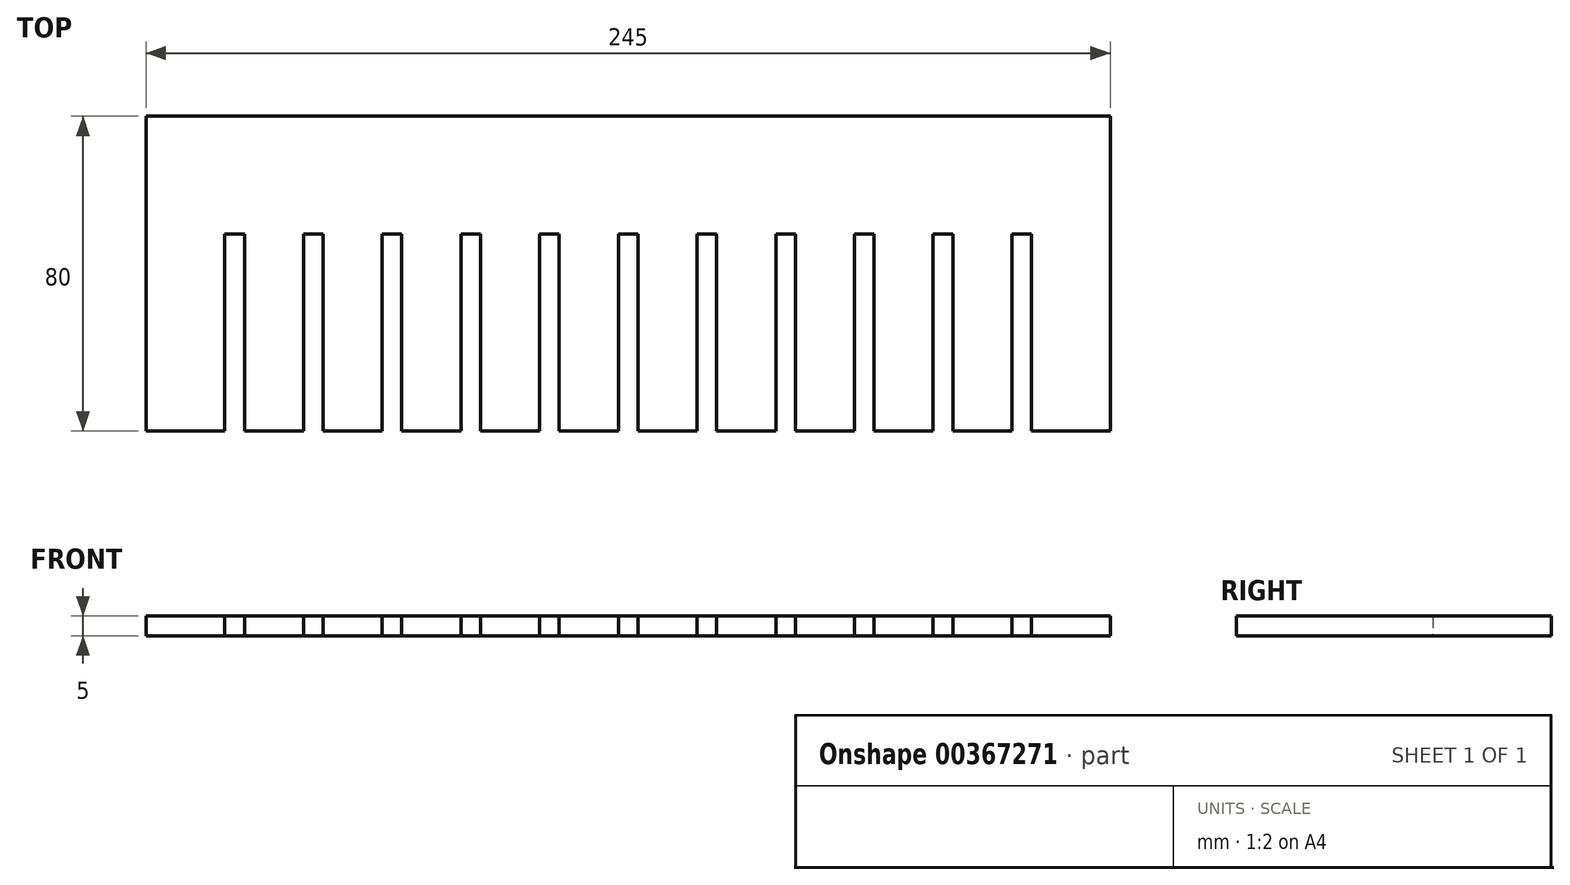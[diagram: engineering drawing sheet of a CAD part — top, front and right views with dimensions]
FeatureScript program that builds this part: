
annotation { "Feature Type Name" : "Feature", "Feature Type Description" : "" }
export const myFeature = defineFeature(function(context is Context, id is Id, definition is map)
    precondition{}
    {
        {
            var Q0;
            Q0=qCreatedBy(makeId("Top.planeOp"),FACE);
            var sketch = newSketch(context, id + "F0", { "sketchPlane" : qUnion([Q0])});
            skLineSegment(sketch, "E0", {"start": v(0, 0) * mm, "end": v(0, 80) * mm});
            skLineSegment(sketch, "E1", {"start": v(0, 0) * mm, "end": v(20, 0) * mm});
            skLineSegment(sketch, "E2", {"start": v(20, 0) * mm, "end": v(20, 50) * mm});
            skLineSegment(sketch, "E3", {"start": v(20, 50) * mm, "end": v(22.5, 50) * mm});
            skLineSegment(sketch, "E4", {"start": v(22.5, 50) * mm, "end": v(25, 50) * mm});
            skLineSegment(sketch, "E5", {"start": v(25, 50) * mm, "end": v(25, 0) * mm});
            skLineSegment(sketch, "E6", {"start": v(25, 0) * mm, "end": v(40, 0) * mm});
            skLineSegment(sketch, "E7", {"start": v(40, 0) * mm, "end": v(40, 50) * mm});
            skLineSegment(sketch, "E8", {"start": v(40, 50) * mm, "end": v(42.5, 50) * mm});
            skLineSegment(sketch, "E9.1.0.0", {"start": v(60, 0) * mm, "end": v(60, 50) * mm});
            skLineSegment(sketch, "E9.1.0.1", {"start": v(45, 0) * mm, "end": v(60, 0) * mm});
            skLineSegment(sketch, "E9.1.0.2", {"start": v(45, 50) * mm, "end": v(45, 0) * mm});
            skLineSegment(sketch, "E9.1.0.3", {"start": v(60, 50) * mm, "end": v(62.5, 50) * mm});
            skLineSegment(sketch, "E9.1.0.4", {"start": v(42.5, 50) * mm, "end": v(45, 50) * mm});
            skLineSegment(sketch, "E9.2.0.0", {"start": v(80, 0) * mm, "end": v(80, 50) * mm});
            skLineSegment(sketch, "E9.2.0.1", {"start": v(65, 0) * mm, "end": v(80, 0) * mm});
            skLineSegment(sketch, "E9.2.0.2", {"start": v(65, 50) * mm, "end": v(65, 0) * mm});
            skLineSegment(sketch, "E9.2.0.3", {"start": v(80, 50) * mm, "end": v(82.5, 50) * mm});
            skLineSegment(sketch, "E9.2.0.4", {"start": v(62.5, 50) * mm, "end": v(65, 50) * mm});
            skLineSegment(sketch, "E9.3.0.0", {"start": v(100, 0) * mm, "end": v(100, 50) * mm});
            skLineSegment(sketch, "E9.3.0.1", {"start": v(85, 0) * mm, "end": v(100, 0) * mm});
            skLineSegment(sketch, "E9.3.0.2", {"start": v(85, 50) * mm, "end": v(85, 0) * mm});
            skLineSegment(sketch, "E9.3.0.3", {"start": v(100, 50) * mm, "end": v(102.5, 50) * mm});
            skLineSegment(sketch, "E9.3.0.4", {"start": v(82.5, 50) * mm, "end": v(85, 50) * mm});
            skLineSegment(sketch, "E9.4.0.0", {"start": v(120, 0) * mm, "end": v(120, 50) * mm});
            skLineSegment(sketch, "E9.4.0.1", {"start": v(105, 0) * mm, "end": v(120, 0) * mm});
            skLineSegment(sketch, "E9.4.0.2", {"start": v(105, 50) * mm, "end": v(105, 0) * mm});
            skLineSegment(sketch, "E9.4.0.3", {"start": v(120, 50) * mm, "end": v(122.5, 50) * mm});
            skLineSegment(sketch, "E9.4.0.4", {"start": v(102.5, 50) * mm, "end": v(105, 50) * mm});
            skLineSegment(sketch, "E9.5.0.0", {"start": v(140, 0) * mm, "end": v(140, 50) * mm});
            skLineSegment(sketch, "E9.5.0.1", {"start": v(125, 0) * mm, "end": v(140, 0) * mm});
            skLineSegment(sketch, "E9.5.0.2", {"start": v(125, 50) * mm, "end": v(125, 0) * mm});
            skLineSegment(sketch, "E9.5.0.3", {"start": v(140, 50) * mm, "end": v(142.5, 50) * mm});
            skLineSegment(sketch, "E9.5.0.4", {"start": v(122.5, 50) * mm, "end": v(125, 50) * mm});
            skLineSegment(sketch, "E9.6.0.0", {"start": v(160, 0) * mm, "end": v(160, 50) * mm});
            skLineSegment(sketch, "E9.6.0.1", {"start": v(145, 0) * mm, "end": v(160, 0) * mm});
            skLineSegment(sketch, "E9.6.0.2", {"start": v(145, 50) * mm, "end": v(145, 0) * mm});
            skLineSegment(sketch, "E9.6.0.3", {"start": v(160, 50) * mm, "end": v(162.5, 50) * mm});
            skLineSegment(sketch, "E9.6.0.4", {"start": v(142.5, 50) * mm, "end": v(145, 50) * mm});
            skLineSegment(sketch, "E9.7.0.0", {"start": v(180, 0) * mm, "end": v(180, 50) * mm});
            skLineSegment(sketch, "E9.7.0.1", {"start": v(165, 0) * mm, "end": v(180, 0) * mm});
            skLineSegment(sketch, "E9.7.0.2", {"start": v(165, 50) * mm, "end": v(165, 0) * mm});
            skLineSegment(sketch, "E9.7.0.3", {"start": v(180, 50) * mm, "end": v(182.5, 50) * mm});
            skLineSegment(sketch, "E9.7.0.4", {"start": v(162.5, 50) * mm, "end": v(165, 50) * mm});
            skLineSegment(sketch, "E9.8.0.0", {"start": v(200, 0) * mm, "end": v(200, 50) * mm});
            skLineSegment(sketch, "E9.8.0.1", {"start": v(185, 0) * mm, "end": v(200, 0) * mm});
            skLineSegment(sketch, "E9.8.0.2", {"start": v(185, 50) * mm, "end": v(185, 0) * mm});
            skLineSegment(sketch, "E9.8.0.3", {"start": v(200, 50) * mm, "end": v(202.5, 50) * mm});
            skLineSegment(sketch, "E9.8.0.4", {"start": v(182.5, 50) * mm, "end": v(185, 50) * mm});
            skLineSegment(sketch, "E9.9.0.0", {"start": v(220, 0) * mm, "end": v(220, 50) * mm});
            skLineSegment(sketch, "E9.9.0.1", {"start": v(205, 0) * mm, "end": v(220, 0) * mm});
            skLineSegment(sketch, "E9.9.0.2", {"start": v(205, 50) * mm, "end": v(205, 0) * mm});
            skLineSegment(sketch, "E9.9.0.3", {"start": v(220, 50) * mm, "end": v(222.5, 50) * mm});
            skLineSegment(sketch, "E9.9.0.4", {"start": v(202.5, 50) * mm, "end": v(205, 50) * mm});
            skLineSegment(sketch, "E9.direction1", {"start": v(25, 0) * mm, "end": v(45, 0) * mm, "construction": true});
            skLineSegment(sketch, "E10", {"start": v(222.5, 50) * mm, "end": v(225, 50) * mm});
            skLineSegment(sketch, "E11", {"start": v(225, 50) * mm, "end": v(225, 0) * mm});
            skLineSegment(sketch, "E12", {"start": v(225, 0) * mm, "end": v(245, 0) * mm});
            skLineSegment(sketch, "E13", {"start": v(245, 0) * mm, "end": v(245, 80) * mm});
            skLineSegment(sketch, "E14", {"start": v(245, 80) * mm, "end": v(0, 80) * mm});
            skSolve(sketch);
        }
        {
            var Q0;
            Q0=makeQuery(id+"F0.imprint","IMPRINT",FACE,{"disambiguationData":[TD([[makeQuery(id+"F0.imprint","IMPRINT",EDGE,{"derivedFrom":sQuery(id+"F0.wireOp",EDGE,"E0")}),-1.0]])]});
            extrude(context, id + "F1", {"entities" : qUnion([Q0]), "depth" : 5 * mm});
        }
    });
